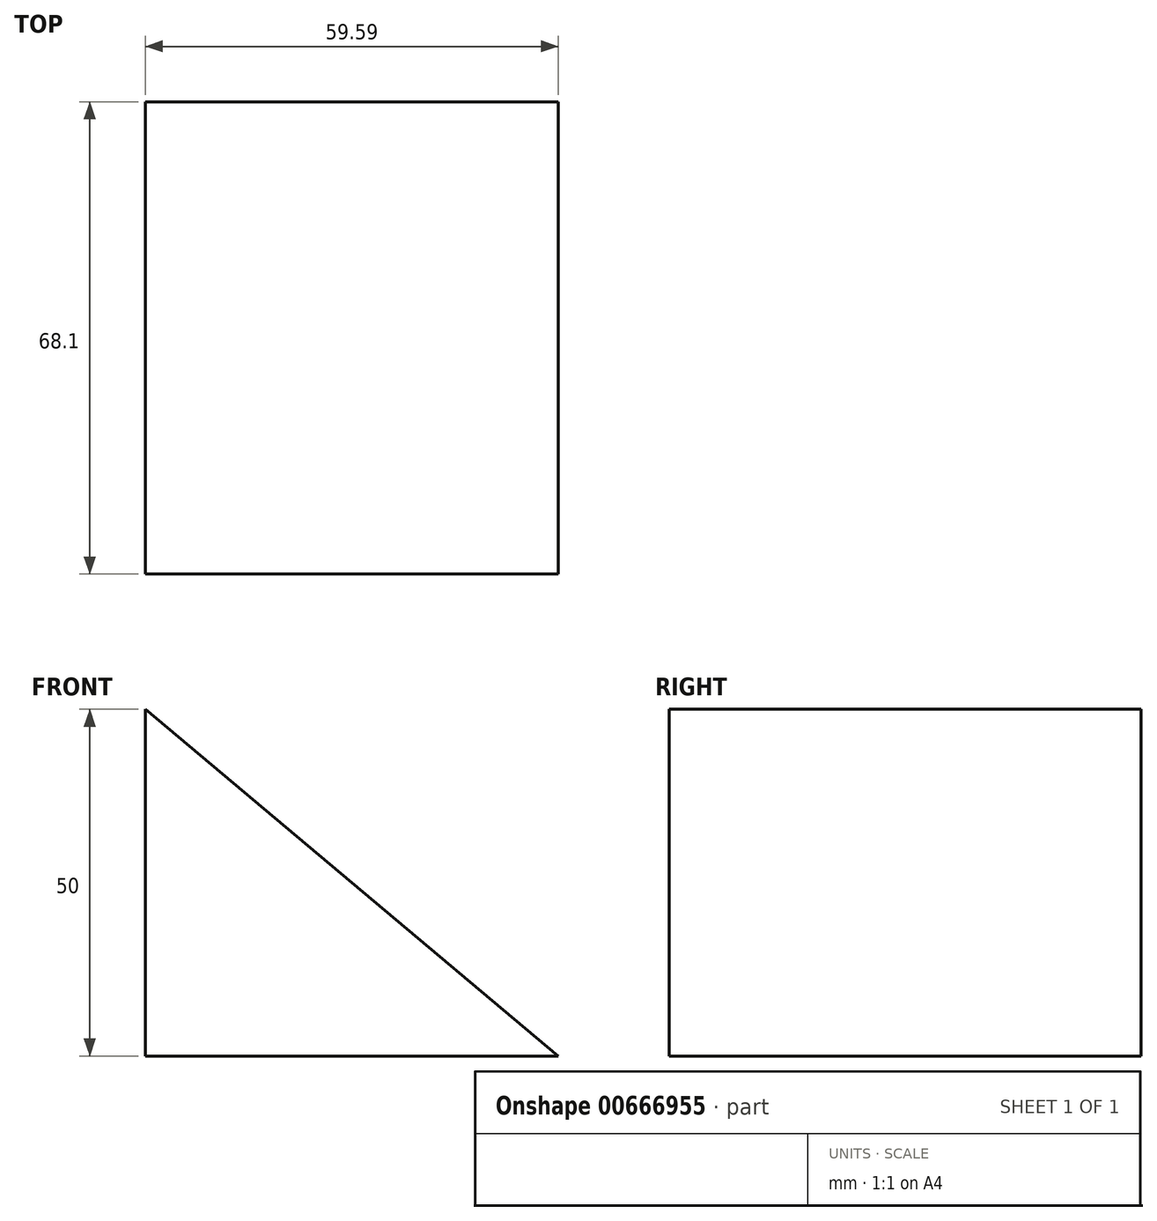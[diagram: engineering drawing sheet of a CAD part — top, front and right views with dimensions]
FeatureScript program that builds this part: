
annotation { "Feature Type Name" : "Feature", "Feature Type Description" : "" }
export const myFeature = defineFeature(function(context is Context, id is Id, definition is map)
    precondition{}
    {
        {
            var Q0;
            Q0=qCreatedBy(makeId("Front.planeOp"),FACE);
            var sketch = newSketch(context, id + "F0", { "sketchPlane" : qUnion([Q0])});
            skLineSegment(sketch, "E0", {"start": v(0, 0) * mm, "end": v(0, 50) * mm});
            skLineSegment(sketch, "E1", {"start": v(0, 50) * mm, "end": v(59.59, 0) * mm});
            skLineSegment(sketch, "E2", {"start": v(0, 0) * mm, "end": v(59.59, 0) * mm});
            skSolve(sketch);
        }
        {
            var Q0;
            Q0=makeQuery(id+"F0.imprint","IMPRINT",FACE,{"disambiguationData":[TD([[makeQuery(id+"F0.imprint","IMPRINT",EDGE,{"derivedFrom":sQuery(id+"F0.wireOp",EDGE,"E0")}),-1.0]])]});
            extrude(context, id + "F1", {"entities" : qUnion([Q0]), "depth" : 68.1 * mm, "offsetDistance" : 25 * mm});
        }
    });
